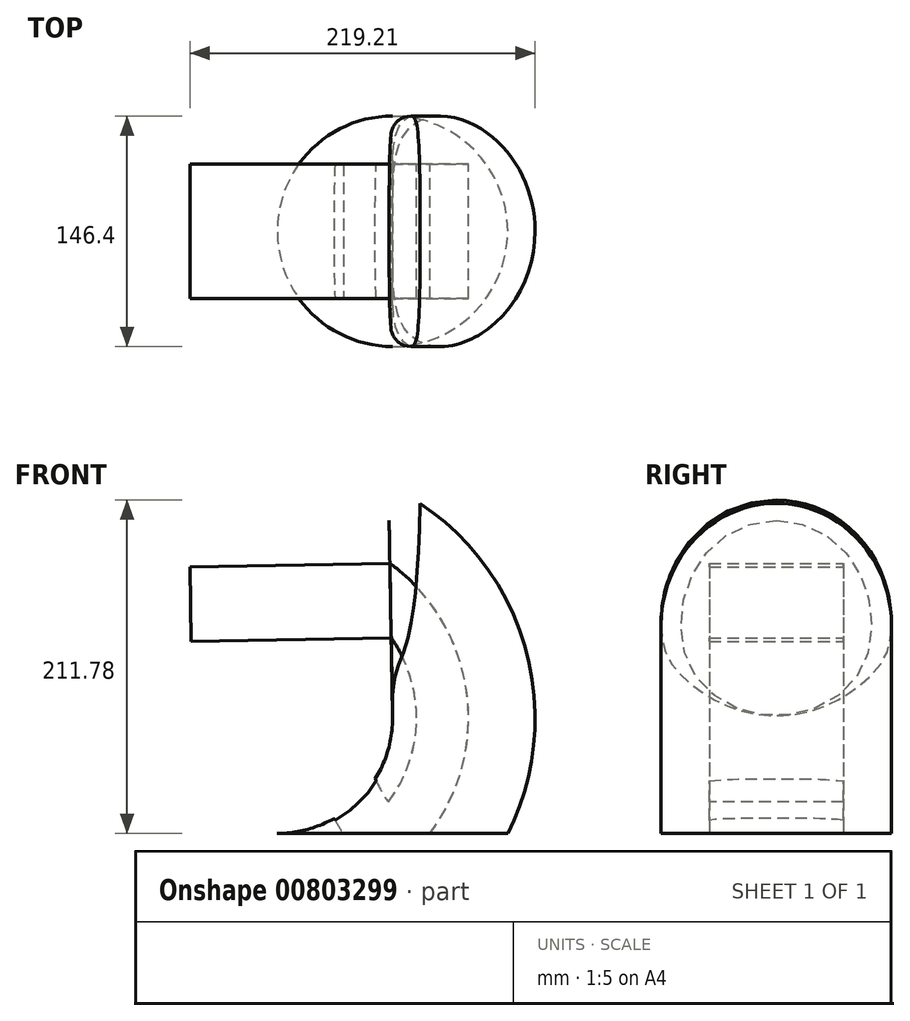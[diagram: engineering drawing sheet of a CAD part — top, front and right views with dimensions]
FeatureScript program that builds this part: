
annotation { "Feature Type Name" : "Feature", "Feature Type Description" : "" }
export const myFeature = defineFeature(function(context is Context, id is Id, definition is map)
    precondition{}
    {
        {
            var Q0;
            Q0=qCreatedBy(makeId("Top.planeOp"),FACE);
            var sketch = newSketch(context, id + "F0", { "sketchPlane" : qUnion([Q0])});
            skCircle(sketch, "E0", {"center": v(0, 0) * mm, "radius": 73.2 * mm});
            skPoint(sketch, "E1", {"position": v(73.2, 0) * mm});
            skPoint(sketch, "E2", {"position": v(-73.2, 0) * mm});
            skPoint(sketch, "E3", {"position": v(0, 73.2) * mm});
            skPoint(sketch, "E4", {"position": v(0, -73.2) * mm});
            skSolve(sketch);
        }
        {
            var Q0;
            Q0=qCreatedBy(makeId("Front.planeOp"),FACE);
            var sketch = newSketch(context, id + "F1", { "sketchPlane" : qUnion([Q0])});
            skArc(sketch, "E5", {"start": v(0, 74.96) * mm, "mid": v(20.06, 21.3) * mm, "end": v(73.25, 0) * mm});
            skArc(sketch, "E6", {"start": v(-72.96, 0) * mm, "mid": v(-20.76, 22.18) * mm, "end": v(0, 74.96) * mm});
            skSolve(sketch);
        }
        {
            var Q0;
            Q0=makeQuery(id+"F0.imprint","IMPRINT",FACE,{"disambiguationData":[TD([[makeQuery(id+"F0.imprint","IMPRINT",EDGE,{"derivedFrom":sQuery(id+"F0.wireOp",EDGE,"E0")}),1.0]])]});
            var Q1;
            Q1=sQuery(id+"F1.wireOp",EDGE,"E6");
            sweep(context, id + "F2", {"profiles" : qUnion([Q0]), "path" : qUnion([Q1])});
        }
        {
            var Q0;
            Q0=makeQuery(id+"F2.opSweep","CAP_FACE",FACE,{"disambiguationData":[OSD([sQuery(id+"F0.wireOp",EDGE,"E0"),sQuery(id+"F1.wireOp",VERTEX,"E6.end")])],"isStart":false});
            var sketch = newSketch(context, id + "F3", { "sketchPlane" : qUnion([Q0])});
            skLineSegment(sketch, "E7.bottom", {"start": v(42.58, 171.57) * mm, "end": v(-42.58, 171.57) * mm});
            skLineSegment(sketch, "E7.top", {"start": v(42.58, 124.26) * mm, "end": v(-42.58, 124.26) * mm});
            skLineSegment(sketch, "E7.left", {"start": v(42.58, 171.57) * mm, "end": v(42.58, 124.26) * mm});
            skLineSegment(sketch, "E7.right", {"start": v(-42.58, 171.57) * mm, "end": v(-42.58, 124.26) * mm});
            skPoint(sketch, "E7.middle", {"position": v(0, 147.91) * mm});
            skSolve(sketch);
        }
        {
            var Q0;
            Q0=makeQuery(id+"F3.imprint","IMPRINT",FACE,{"disambiguationData":[TD([[makeQuery(id+"F3.imprint","IMPRINT",EDGE,{"derivedFrom":sQuery(id+"F3.wireOp",EDGE,"E7.bottom")}),1.0]])]});
            var Q1;
            Q1=sQuery(id+"F1.wireOp",EDGE,"E6");
            sweep(context, id + "F4", {"operationType" : NewBodyOperationType.REMOVE, "profiles" : qUnion([Q0]), "path" : qUnion([Q1])});
        }
        {
            var Q0;
            Q0=makeQuery(id+"F3.imprint","IMPRINT",FACE,{"disambiguationData":[TD([[makeQuery(id+"F3.imprint","IMPRINT",EDGE,{"derivedFrom":sQuery(id+"F3.wireOp",EDGE,"E7.bottom")}),1.0]])]});
            var Q1;
            Q1=sQuery(id+"F1.wireOp",EDGE,"E5");
            sweep(context, id + "F5", {"operationType" : NewBodyOperationType.REMOVE, "profiles" : qUnion([Q0]), "path" : qUnion([Q1])});
        }
        {
            var Q0;
            Q0=makeQuery(id+"F2.opSweep","CAP_EDGE",EDGE,{"disambiguationData":[OSD([sQuery(id+"F0.wireOp",EDGE,"E0"),sQuery(id+"F1.wireOp",VERTEX,"E6.end")])],"isStart":false});
            fillet(context, id + "F6", {"entities" : qUnion([Q0]), "radius" : 12.7 * mm, "tangentPropagation" : true, "allowEdgeOverflow" : false});
        }
        {
            var Q0;
            Q0=makeQuery(id+"F3.imprint","IMPRINT",FACE,{"disambiguationData":[TD([[makeQuery(id+"F3.imprint","IMPRINT",EDGE,{"derivedFrom":sQuery(id+"F3.wireOp",EDGE,"E7.bottom")}),1.0]])]});
            extrude(context, id + "F7", {"entities" : qUnion([Q0]), "depth" : 127 * mm, "offsetDistance" : 25.4 * mm});
        }
    });
